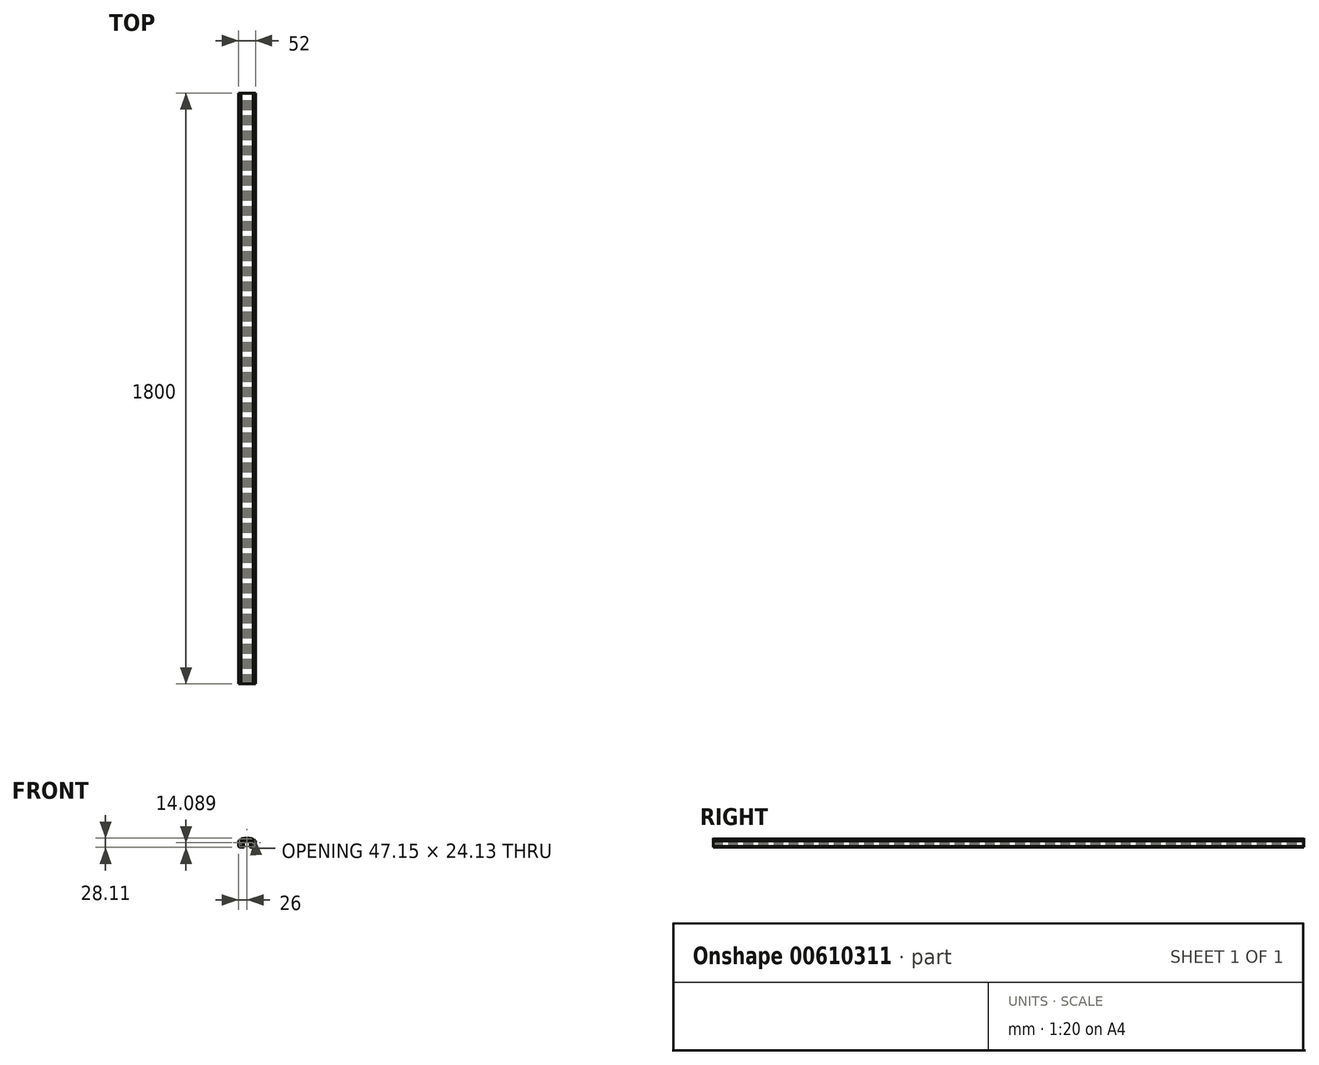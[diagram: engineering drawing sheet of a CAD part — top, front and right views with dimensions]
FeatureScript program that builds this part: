
annotation { "Feature Type Name" : "Feature", "Feature Type Description" : "" }
export const myFeature = defineFeature(function(context is Context, id is Id, definition is map)
    precondition{}
    {
        {
            var Q0;
            Q0=qCreatedBy(makeId("Front.planeOp"),FACE);
            var sketch = newSketch(context, id + "F0", { "sketchPlane" : qUnion([Q0])});
            skLineSegment(sketch, "E0", {"start": v(-8, 0.8) * mm, "end": v(8.09, 0.8) * mm});
            skLineSegment(sketch, "E1", {"start": v(-8, 0.8) * mm, "end": v(-8, -2.25) * mm});
            skLineSegment(sketch, "E2", {"start": v(-8, -2.25) * mm, "end": v(-5.3, -2.25) * mm});
            skLineSegment(sketch, "E3", {"start": v(-5.3, -2.25) * mm, "end": v(-6.6, -4.95) * mm});
            skLineSegment(sketch, "E4", {"start": v(-6.6, -4.95) * mm, "end": v(-11.46, -4.95) * mm});
            skLineSegment(sketch, "E5", {"start": v(-11.46, -4.95) * mm, "end": v(-11.46, -8.47) * mm});
            skLineSegment(sketch, "E6", {"start": v(-11.46, -8.47) * mm, "end": v(-9.83, -8.47) * mm});
            skLineSegment(sketch, "E7", {"start": v(-9.83, -8.47) * mm, "end": v(-11.46, -14.95) * mm});
            skLineSegment(sketch, "E8", {"start": v(-11.46, -14.95) * mm, "end": v(-10.37, -14.95) * mm});
            skLineSegment(sketch, "E9", {"start": v(-13.53, -4.95) * mm, "end": v(-13.53, -10.76) * mm});
            skLineSegment(sketch, "E10", {"start": v(-13.53, -4.95) * mm, "end": v(-11.46, -4.95) * mm, "construction": true});
            skLineSegment(sketch, "E11", {"start": v(-13.53, -10.76) * mm, "end": v(-12.44, -10.76) * mm});
            skLineSegment(sketch, "E12", {"start": v(-12.44, -10.76) * mm, "end": v(-14.36, -16.98) * mm});
            skLineSegment(sketch, "E13", {"start": v(-14.36, -16.98) * mm, "end": v(-22.43, -16.98) * mm});
            skLineSegment(sketch, "E14", {"start": v(-22.43, -16.98) * mm, "end": v(-23.58, -15.88) * mm});
            skLineSegment(sketch, "E15", {"start": v(-23.58, -15.88) * mm, "end": v(-23.58, -0.99) * mm});
            skFitSpline(sketch, "E16", {"points": [v(-23.58, -0.99) * mm, v(-20.66, 1.27) * mm, v(-16.66, 3.5) * mm], "startDerivative": vector(5.82, 4.9) * mm, "endDerivative": vector(7.98, 4.1) * mm});
            skLineSegment(sketch, "E17", {"start": v(-16.66, 3.5) * mm, "end": v(-16.66, 4.58) * mm});
            skFitSpline(sketch, "E18", {"points": [v(-16.66, 4.58) * mm, v(-13.13, 5.78) * mm, v(-4.41, 6.92) * mm, v(0, 7.14) * mm], "startDerivative": vector(10.72, 4.58) * mm, "endDerivative": vector(12.81, 0.4) * mm});
            skFitSpline(sketch, "E19", {"points": [v(-18.58, 6.7) * mm, v(-14.22, 7.85) * mm, v(-5.77, 8.94) * mm, v(0, 9.1) * mm], "startDerivative": vector(13.63, 4.15) * mm, "endDerivative": vector(16.55, 0.04) * mm});
            skLineSegment(sketch, "E20", {"start": v(-18.58, 6.7) * mm, "end": v(-18.58, 5.13) * mm});
            skFitSpline(sketch, "E21", {"points": [v(-26, 0.41) * mm, v(-23.8, 2.15) * mm, v(-20.36, 4.17) * mm, v(-18.58, 5.13) * mm], "startDerivative": vector(6, 5.21) * mm, "endDerivative": vector(5.7, 3.07) * mm});
            skLineSegment(sketch, "E22", {"start": v(-26, 0.41) * mm, "end": v(-26, -16.17) * mm});
            skLineSegment(sketch, "E23", {"start": v(-26, -16.17) * mm, "end": v(-23.24, -19) * mm});
            skLineSegment(sketch, "E24", {"start": v(-23.24, -19) * mm, "end": v(-9.45, -19) * mm});
            skLineSegment(sketch, "E25", {"start": v(0.05, 0.8) * mm, "end": v(0.05, 2.38) * mm});
            skLineSegment(sketch, "E26", {"start": v(0.05, 2.38) * mm, "end": v(-9.1, 2.38) * mm});
            skLineSegment(sketch, "E27", {"start": v(-9.1, 2.38) * mm, "end": v(-10.17, 2.38) * mm, "construction": true});
            skLineSegment(sketch, "E28", {"start": v(-12.37, 2.38) * mm, "end": v(-10.17, 2.38) * mm});
            skArc(sketch, "E29", {"start": v(-10.17, 2.38) * mm, "mid": v(-9.63, 1.84) * mm, "end": v(-9.1, 2.38) * mm});
            skLineSegment(sketch, "E30", {"start": v(-12.37, 2.38) * mm, "end": v(-12.37, 0.6) * mm, "construction": true});
            skLineSegment(sketch, "E31", {"start": v(-11.58, 0) * mm, "end": v(-10.2, 0) * mm});
            skArc(sketch, "E32", {"start": v(-12.37, 2.38) * mm, "mid": v(-13.26, 1.5) * mm, "end": v(-12.37, 0.6) * mm});
            skArc(sketch, "E33", {"start": v(-13.37, -0.97) * mm, "mid": v(-11.12, -2.68) * mm, "end": v(-10.2, 0) * mm});
            skFitSpline(sketch, "E34", {"points": [v(-12.37, 0.6) * mm, v(-11.58, 0.46) * mm, v(-10.2, 0) * mm], "startDerivative": vector(1.74, -0.23) * mm, "endDerivative": vector(2.55, -0.94) * mm});
            skLineSegment(sketch, "E35", {"start": v(-13.37, -0.97) * mm, "end": v(-15.69, -0.97) * mm});
            skArc(sketch, "E36", {"start": v(-13.37, -0.97) * mm, "mid": v(-14.53, 0.2) * mm, "end": v(-15.69, -0.97) * mm});
            skArc(sketch, "E37", {"start": v(-15.69, -0.97) * mm, "mid": v(-15.2, -3.28) * mm, "end": v(-13.53, -4.95) * mm});
            skLineSegment(sketch, "E38", {"start": v(-10.37, -14.95) * mm, "end": v(-6.59, -13.58) * mm});
            skLineSegment(sketch, "E39", {"start": v(-6.59, -13.58) * mm, "end": v(-7.36, -16.85) * mm});
            skLineSegment(sketch, "E40", {"start": v(-7.36, -16.85) * mm, "end": v(-9.45, -16.85) * mm});
            skLineSegment(sketch, "E41", {"start": v(-9.45, -19) * mm, "end": v(-9.45, -16.85) * mm});
            skLineSegment(sketch, "E42", {"start": v(0, 7.14) * mm, "end": v(0, 9.1) * mm});
            skLineSegment(sketch, "E43", {"start": v(0, 7.14) * mm, "end": v(0.05, 2.38) * mm});
            skLineSegment(sketch, "E44", {"start": v(-9.45, -19) * mm, "end": v(0.05, -19) * mm, "construction": true});
            skLineSegment(sketch, "E45", {"start": v(0.05, -19) * mm, "end": v(0, 0) * mm, "construction": true});
            skSolve(sketch);
        }
        {
            var Q0;
            {var subQ0=sQuery(id+"F0.wireOp",EDGE,"E1");Q0=makeQuery(id+"F0.imprint","IMPRINT",FACE,{"disambiguationData":[TD([[makeQuery(id+"F0.imprint","IMPRINT",EDGE,{"derivedFrom":subQ0}),-1.0]])]});}
            var Q1;
            Q1=makeQuery(id+"F0.imprint","IMPRINT",FACE,{"disambiguationData":[TD([[makeQuery(id+"F0.imprint","IMPRINT",EDGE,{"derivedFrom":sQuery(id+"F0.wireOp",EDGE,"E35")}),-1.0]])]});
            extrude(context, id + "F1", {"entities" : qUnion([Q0, Q1]), "depth" : 1800 * mm, "offsetDistance" : 25 * mm});
        }
        {
            var Q0;
            Q0=makeQuery(id+"F1.opExtrude","SWEPT_BODY",BODY,{"disambiguationData":[OSD([sQuery(id+"F0.wireOp",EDGE,"E0"),sQuery(id+"F0.wireOp",EDGE,"E1"),sQuery(id+"F0.wireOp",EDGE,"E2"),sQuery(id+"F0.wireOp",EDGE,"E3"),sQuery(id+"F0.wireOp",EDGE,"E4"),sQuery(id+"F0.wireOp",EDGE,"E5"),sQuery(id+"F0.wireOp",EDGE,"E6"),sQuery(id+"F0.wireOp",EDGE,"E7"),sQuery(id+"F0.wireOp",EDGE,"E8"),sQuery(id+"F0.wireOp",EDGE,"E9"),sQuery(id+"F0.wireOp",EDGE,"E11"),sQuery(id+"F0.wireOp",EDGE,"E12"),sQuery(id+"F0.wireOp",EDGE,"E13"),sQuery(id+"F0.wireOp",EDGE,"E14"),sQuery(id+"F0.wireOp",EDGE,"E15"),sQuery(id+"F0.wireOp",EDGE,"E16"),sQuery(id+"F0.wireOp",EDGE,"E17"),sQuery(id+"F0.wireOp",EDGE,"E18"),sQuery(id+"F0.wireOp",EDGE,"E19"),sQuery(id+"F0.wireOp",EDGE,"E20"),sQuery(id+"F0.wireOp",EDGE,"E21"),sQuery(id+"F0.wireOp",EDGE,"E22"),sQuery(id+"F0.wireOp",EDGE,"E23"),sQuery(id+"F0.wireOp",EDGE,"E24"),sQuery(id+"F0.wireOp",EDGE,"E25"),sQuery(id+"F0.wireOp",EDGE,"E26"),sQuery(id+"F0.wireOp",EDGE,"E28"),sQuery(id+"F0.wireOp",EDGE,"E29"),sQuery(id+"F0.wireOp",EDGE,"E32"),sQuery(id+"F0.wireOp",EDGE,"E33"),sQuery(id+"F0.wireOp",EDGE,"E34"),sQuery(id+"F0.wireOp",EDGE,"E35"),sQuery(id+"F0.wireOp",EDGE,"E37"),sQuery(id+"F0.wireOp",EDGE,"E38"),sQuery(id+"F0.wireOp",EDGE,"E39"),sQuery(id+"F0.wireOp",EDGE,"E40"),sQuery(id+"F0.wireOp",EDGE,"E41"),sQuery(id+"F0.wireOp",EDGE,"E42")])]});
            var Q1;
            Q1=qCreatedBy(makeId("Right.planeOp"),FACE);
            mirror(context, id + "F2", {"operationType" : NewBodyOperationType.ADD, "entities" : qUnion([Q0]), "mirrorPlane" : qUnion([Q1])});
        }
    });
